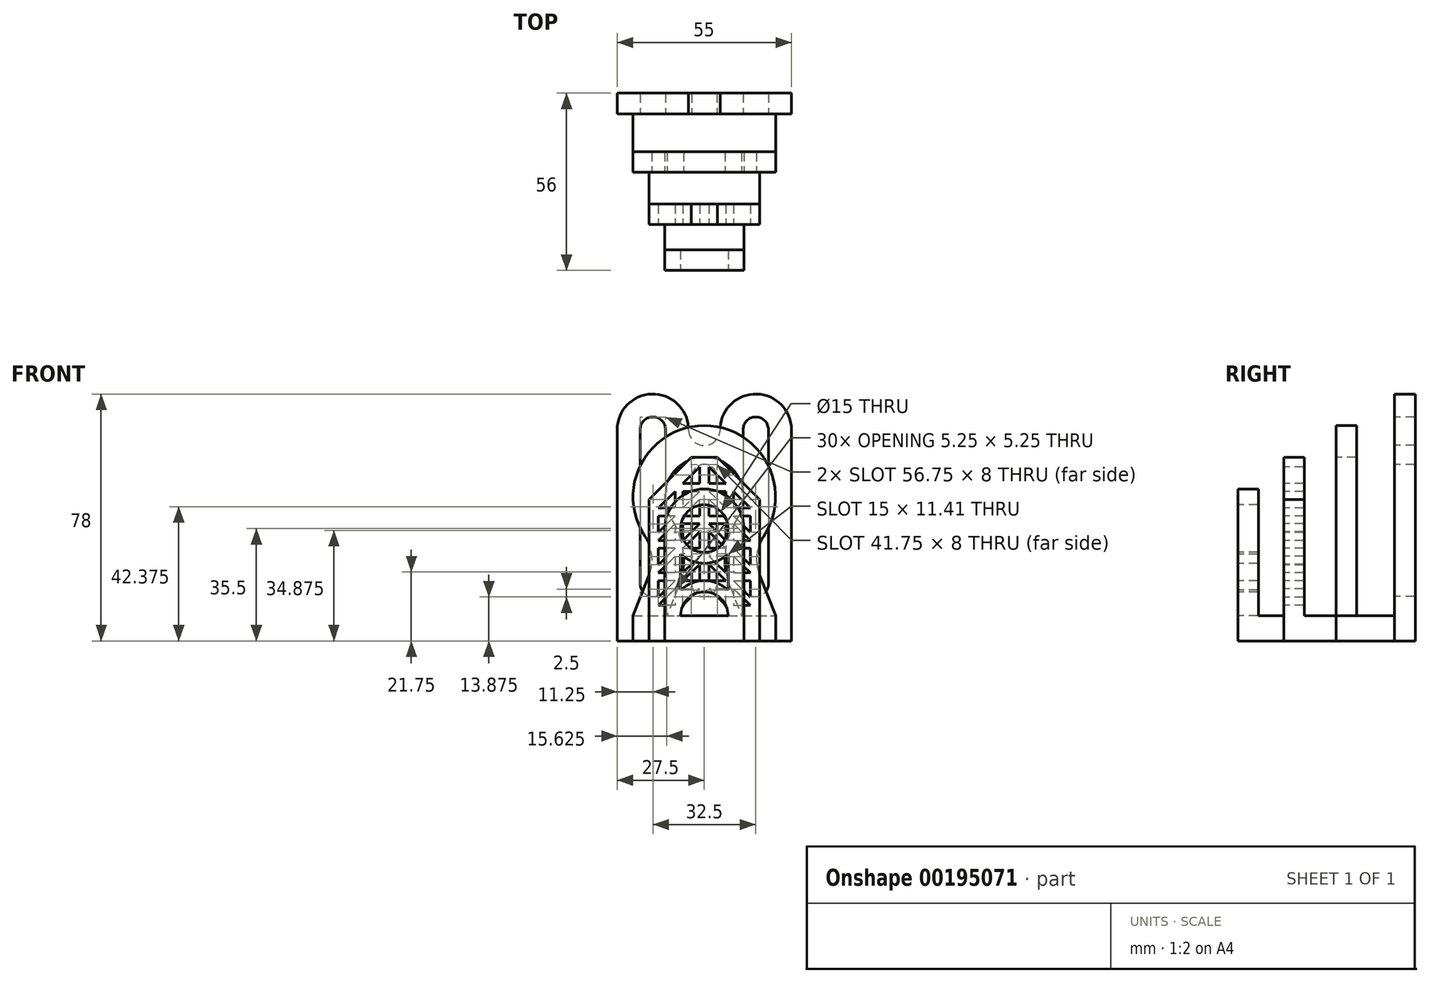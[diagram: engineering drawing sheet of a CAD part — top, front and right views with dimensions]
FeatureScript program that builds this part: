
annotation { "Feature Type Name" : "Feature", "Feature Type Description" : "" }
export const myFeature = defineFeature(function(context is Context, id is Id, definition is map)
    precondition{}
    {
        {
            var Q0;
            Q0=qCreatedBy(makeId("Front.planeOp"),FACE);
            var sketch = newSketch(context, id + "F0", { "sketchPlane" : qUnion([Q0])});
            skLineSegment(sketch, "E0.bottom", {"start": v(-12.5, 0) * mm, "end": v(-7.5, 0) * mm});
            skLineSegment(sketch, "E0.left", {"start": v(-12.5, 0) * mm, "end": v(-12.5, 27.5) * mm});
            skLineSegment(sketch, "E0.right", {"start": v(12.5, 0) * mm, "end": v(12.5, 27.5) * mm});
            skPoint(sketch, "E1", {"position": v(0, 0) * mm});
            skArc(sketch, "E2", {"start": v(12.5, 27.5) * mm, "mid": v(0, 40) * mm, "end": v(-12.5, 27.5) * mm});
            skPoint(sketch, "E3", {"position": v(0, 40) * mm});
            skCircle(sketch, "E4", {"center": v(0, 27.5) * mm, "radius": 7.5 * mm});
            skArc(sketch, "E5", {"start": v(7.5, 0) * mm, "mid": v(0, 7.5) * mm, "end": v(-7.5, 0) * mm});
            skLineSegment(sketch, "E6", {"start": v(-7.5, 27.5) * mm, "end": v(-7.5, 19.45) * mm, "construction": true});
            skLineSegment(sketch, "E7", {"start": v(0, 13.75) * mm, "end": v(-7.5, 13.75) * mm, "construction": true});
            skLineSegment(sketch, "E8", {"start": v(0, 27.5) * mm, "end": v(0, 0) * mm, "construction": true});
            skArc(sketch, "E9", {"start": v(-7.5, 19.45) * mm, "mid": v(-4.03, 17.26) * mm, "end": v(0, 16.5) * mm});
            skPoint(sketch, "E10", {"position": v(0, 20) * mm});
            skLineSegment(sketch, "E11", {"start": v(-7.5, 19.45) * mm, "end": v(-7.5, 13.75) * mm});
            skLineSegment(sketch, "E12", {"start": v(-7.5, 13.75) * mm, "end": v(-7.5, 8.05) * mm});
            skArc(sketch, "E13.MirrorCS", {"start": v(-7.5, 8.05) * mm, "mid": v(-4.03, 10.24) * mm, "end": v(0, 11) * mm});
            skLineSegment(sketch, "E14", {"start": v(-7.5, 8.05) * mm, "end": v(-7.5, 0) * mm, "construction": true});
            skArc(sketch, "E15.MirrorCS", {"start": v(7.5, 19.45) * mm, "mid": v(4.03, 17.26) * mm, "end": v(0, 16.5) * mm});
            skLineSegment(sketch, "E16.MirrorCS", {"start": v(7.5, 19.45) * mm, "end": v(7.5, 13.75) * mm});
            skLineSegment(sketch, "E17.MirrorCS", {"start": v(7.5, 13.75) * mm, "end": v(7.5, 8.05) * mm});
            skArc(sketch, "E18.MirrorCS", {"start": v(7.5, 8.05) * mm, "mid": v(4.03, 10.24) * mm, "end": v(0, 11) * mm});
            skLineSegment(sketch, "E19.trimOffspring", {"start": v(7.5, 0) * mm, "end": v(12.5, 0) * mm});
            skSolve(sketch);
        }
        {
            var Q0;
            Q0 = qSketchRegion(id + "F0", true);
            extrude(context, id + "F1", {"entities" : qUnion([Q0]), "oppositeDirection" : true, "depth" : 6.5 * mm});
        }
        {
            var Q0;
            Q0=makeQuery(id+"F1.opExtrude","CAP_FACE",FACE,{"disambiguationData":[OSD([sQuery(id+"F0.wireOp",EDGE,"E0.bottom"),sQuery(id+"F0.wireOp",EDGE,"E0.top"),sQuery(id+"F0.wireOp",EDGE,"E0.left"),sQuery(id+"F0.wireOp",EDGE,"E0.right")])],"isStart":false});
            cPlane(context, id + "F2", {"entities" : qUnion([Q0]), "cplaneType" : CPlaneType.OFFSET, "offset" : 8 * mm, "width" : 150 * mm, "height" : 150 * mm});
        }
        {
            var Q0;
            Q0=qCreatedBy(id+"F2.planeOp",FACE);
            var sketch = newSketch(context, id + "F3", { "sketchPlane" : qUnion([Q0])});
            skLineSegment(sketch, "E20.bottom", {"start": v(17.5, 0) * mm, "end": v(-17.5, 0) * mm});
            skPoint(sketch, "E21", {"position": v(0, 0) * mm});
            skLineSegment(sketch, "E22", {"start": v(-4.16, 50) * mm, "end": v(-17.5, 36.66) * mm});
            skLineSegment(sketch, "E23", {"start": v(-17.5, 36.66) * mm, "end": v(-17.5, 0) * mm});
            skPoint(sketch, "E24", {"position": v(-17.5, 50) * mm});
            skLineSegment(sketch, "E25", {"start": v(-4.16, 50) * mm, "end": v(0, 50) * mm});
            skLineSegment(sketch, "E26", {"start": v(-6.75, 39.25) * mm, "end": v(-1.5, 39.25) * mm});
            skLineSegment(sketch, "E27", {"start": v(-1.5, 39.25) * mm, "end": v(-6.75, 34) * mm});
            skLineSegment(sketch, "E28", {"start": v(-6.75, 34) * mm, "end": v(-6.75, 39.25) * mm});
            skLineSegment(sketch, "E29", {"start": v(-9.25, 39.25) * mm, "end": v(-9.25, 34) * mm});
            skLineSegment(sketch, "E30", {"start": v(-9.25, 34) * mm, "end": v(-14.5, 34) * mm});
            skLineSegment(sketch, "E31", {"start": v(-14.5, 34) * mm, "end": v(-9.25, 39.25) * mm});
            skLineSegment(sketch, "E32", {"start": v(-9.25, 31.5) * mm, "end": v(-14.5, 31.5) * mm});
            skLineSegment(sketch, "E33", {"start": v(-14.5, 31.5) * mm, "end": v(-14.5, 26.25) * mm});
            skLineSegment(sketch, "E34", {"start": v(-14.5, 26.25) * mm, "end": v(-9.25, 31.5) * mm});
            skLineSegment(sketch, "E35", {"start": v(-6.75, 41.75) * mm, "end": v(-1.5, 41.75) * mm});
            skLineSegment(sketch, "E36", {"start": v(-1.5, 41.75) * mm, "end": v(-1.5, 47) * mm});
            skLineSegment(sketch, "E37", {"start": v(-1.5, 47) * mm, "end": v(-6.75, 41.75) * mm});
            skLineSegment(sketch, "E38", {"start": v(-6.75, 34) * mm, "end": v(-9.25, 31.5) * mm, "construction": true});
            skLineSegment(sketch, "E39", {"start": v(-6.75, 41.75) * mm, "end": v(-9.25, 39.25) * mm, "construction": true});
            skLineSegment(sketch, "E40.direction1", {"start": v(-6.75, 41.75) * mm, "end": v(-6.75, 31.5) * mm, "construction": true});
            skLineSegment(sketch, "E41.0.1.0", {"start": v(-1.5, 36.75) * mm, "end": v(-6.75, 31.5) * mm});
            skLineSegment(sketch, "E41.3.1.0", {"start": v(-1.5, 31.5) * mm, "end": v(-1.5, 36.75) * mm});
            skLineSegment(sketch, "E41.6.1.0", {"start": v(-6.75, 31.5) * mm, "end": v(-1.5, 31.5) * mm});
            skLineSegment(sketch, "E41.9.1.0", {"start": v(-6.75, 29) * mm, "end": v(-1.5, 29) * mm});
            skLineSegment(sketch, "E41.12.1.0", {"start": v(-1.5, 29) * mm, "end": v(-6.75, 23.75) * mm});
            skLineSegment(sketch, "E41.15.1.0", {"start": v(-6.75, 23.75) * mm, "end": v(-6.75, 29) * mm});
            skLineSegment(sketch, "E41.18.1.0", {"start": v(-9.25, 29) * mm, "end": v(-9.25, 23.75) * mm});
            skLineSegment(sketch, "E41.21.1.0", {"start": v(-14.5, 23.75) * mm, "end": v(-9.25, 29) * mm});
            skLineSegment(sketch, "E41.24.1.0", {"start": v(-9.25, 23.75) * mm, "end": v(-14.5, 23.75) * mm});
            skLineSegment(sketch, "E41.27.1.0", {"start": v(-9.25, 21.25) * mm, "end": v(-14.5, 21.25) * mm});
            skLineSegment(sketch, "E41.30.1.0", {"start": v(-14.5, 16) * mm, "end": v(-9.25, 21.25) * mm});
            skLineSegment(sketch, "E41.33.1.0", {"start": v(-14.5, 21.25) * mm, "end": v(-14.5, 16) * mm});
            skLineSegment(sketch, "E41.0.2.0", {"start": v(-1.5, 26.5) * mm, "end": v(-6.75, 21.25) * mm});
            skLineSegment(sketch, "E41.3.2.0", {"start": v(-1.5, 21.25) * mm, "end": v(-1.5, 26.5) * mm});
            skLineSegment(sketch, "E41.6.2.0", {"start": v(-6.75, 21.25) * mm, "end": v(-1.5, 21.25) * mm});
            skLineSegment(sketch, "E41.9.2.0", {"start": v(-6.75, 18.75) * mm, "end": v(-1.5, 18.75) * mm});
            skLineSegment(sketch, "E41.12.2.0", {"start": v(-1.5, 18.75) * mm, "end": v(-6.75, 13.5) * mm});
            skLineSegment(sketch, "E41.15.2.0", {"start": v(-6.75, 13.5) * mm, "end": v(-6.75, 18.75) * mm});
            skLineSegment(sketch, "E41.18.2.0", {"start": v(-9.25, 18.75) * mm, "end": v(-9.25, 13.5) * mm});
            skLineSegment(sketch, "E41.21.2.0", {"start": v(-14.5, 13.5) * mm, "end": v(-9.25, 18.75) * mm});
            skLineSegment(sketch, "E41.24.2.0", {"start": v(-9.25, 13.5) * mm, "end": v(-14.5, 13.5) * mm});
            skLineSegment(sketch, "E41.27.2.0", {"start": v(-9.25, 11) * mm, "end": v(-14.5, 11) * mm});
            skLineSegment(sketch, "E41.30.2.0", {"start": v(-14.5, 5.75) * mm, "end": v(-9.25, 11) * mm});
            skLineSegment(sketch, "E41.33.2.0", {"start": v(-14.5, 11) * mm, "end": v(-14.5, 5.75) * mm});
            skLineSegment(sketch, "E41.0.3.0", {"start": v(-1.5, 16.25) * mm, "end": v(-6.75, 11) * mm});
            skLineSegment(sketch, "E41.3.3.0", {"start": v(-1.5, 11) * mm, "end": v(-1.5, 16.25) * mm});
            skLineSegment(sketch, "E41.6.3.0", {"start": v(-6.75, 11) * mm, "end": v(-1.5, 11) * mm});
            skLineSegment(sketch, "E41.9.3.0", {"start": v(-6.75, 8.5) * mm, "end": v(-1.5, 8.5) * mm});
            skLineSegment(sketch, "E41.12.3.0", {"start": v(-1.5, 8.5) * mm, "end": v(-6.75, 3.25) * mm});
            skLineSegment(sketch, "E41.15.3.0", {"start": v(-6.75, 3.25) * mm, "end": v(-6.75, 8.5) * mm});
            skLineSegment(sketch, "E41.18.3.0", {"start": v(-9.25, 8.5) * mm, "end": v(-9.25, 3.25) * mm});
            skLineSegment(sketch, "E41.21.3.0", {"start": v(-14.5, 3.25) * mm, "end": v(-9.25, 8.5) * mm});
            skLineSegment(sketch, "E41.24.3.0", {"start": v(-9.25, 3.25) * mm, "end": v(-14.5, 3.25) * mm});
            skLineSegment(sketch, "E42.MirrorCS", {"start": v(4.16, 50) * mm, "end": v(0, 50) * mm});
            skLineSegment(sketch, "E43.MirrorCS", {"start": v(4.16, 50) * mm, "end": v(17.5, 36.66) * mm});
            skLineSegment(sketch, "E44.MirrorCS", {"start": v(17.5, 36.66) * mm, "end": v(17.5, 0) * mm});
            skLineSegment(sketch, "E45.MirrorCS", {"start": v(1.5, 47) * mm, "end": v(6.75, 41.75) * mm});
            skLineSegment(sketch, "E46.MirrorCS", {"start": v(1.5, 41.75) * mm, "end": v(1.5, 47) * mm});
            skLineSegment(sketch, "E47.MirrorCS", {"start": v(6.75, 41.75) * mm, "end": v(1.5, 41.75) * mm});
            skLineSegment(sketch, "E48.MirrorCS", {"start": v(6.75, 39.25) * mm, "end": v(1.5, 39.25) * mm});
            skLineSegment(sketch, "E49.MirrorCS", {"start": v(1.5, 39.25) * mm, "end": v(6.75, 34) * mm});
            skLineSegment(sketch, "E50.MirrorCS", {"start": v(9.25, 39.25) * mm, "end": v(9.25, 34) * mm});
            skLineSegment(sketch, "E51.MirrorCS", {"start": v(14.5, 34) * mm, "end": v(9.25, 39.25) * mm});
            skLineSegment(sketch, "E52.MirrorCS", {"start": v(9.25, 34) * mm, "end": v(14.5, 34) * mm});
            skLineSegment(sketch, "E53.MirrorCS", {"start": v(1.5, 36.75) * mm, "end": v(6.75, 31.5) * mm});
            skLineSegment(sketch, "E54.MirrorCS", {"start": v(1.5, 31.5) * mm, "end": v(1.5, 36.75) * mm});
            skLineSegment(sketch, "E55.MirrorCS", {"start": v(6.75, 31.5) * mm, "end": v(1.5, 31.5) * mm});
            skLineSegment(sketch, "E56.MirrorCS", {"start": v(9.25, 31.5) * mm, "end": v(14.5, 31.5) * mm});
            skLineSegment(sketch, "E57.MirrorCS", {"start": v(14.5, 26.25) * mm, "end": v(9.25, 31.5) * mm});
            skLineSegment(sketch, "E58.MirrorCS", {"start": v(14.5, 31.5) * mm, "end": v(14.5, 26.25) * mm});
            skLineSegment(sketch, "E59.MirrorCS", {"start": v(6.75, 29) * mm, "end": v(1.5, 29) * mm});
            skLineSegment(sketch, "E60.MirrorCS", {"start": v(1.5, 29) * mm, "end": v(6.75, 23.75) * mm});
            skLineSegment(sketch, "E61.MirrorCS", {"start": v(6.75, 23.75) * mm, "end": v(6.75, 29) * mm});
            skLineSegment(sketch, "E62.MirrorCS", {"start": v(9.25, 29) * mm, "end": v(9.25, 23.75) * mm});
            skLineSegment(sketch, "E63.MirrorCS", {"start": v(14.5, 23.75) * mm, "end": v(9.25, 29) * mm});
            skLineSegment(sketch, "E64.MirrorCS", {"start": v(9.25, 23.75) * mm, "end": v(14.5, 23.75) * mm});
            skLineSegment(sketch, "E65.MirrorCS", {"start": v(1.5, 26.5) * mm, "end": v(6.75, 21.25) * mm});
            skLineSegment(sketch, "E66.MirrorCS", {"start": v(1.5, 21.25) * mm, "end": v(1.5, 26.5) * mm});
            skLineSegment(sketch, "E67.MirrorCS", {"start": v(6.75, 21.25) * mm, "end": v(1.5, 21.25) * mm});
            skLineSegment(sketch, "E68.MirrorCS", {"start": v(9.25, 21.25) * mm, "end": v(14.5, 21.25) * mm});
            skLineSegment(sketch, "E69.MirrorCS", {"start": v(14.5, 16) * mm, "end": v(9.25, 21.25) * mm});
            skLineSegment(sketch, "E70.MirrorCS", {"start": v(14.5, 21.25) * mm, "end": v(14.5, 16) * mm});
            skLineSegment(sketch, "E71.MirrorCS", {"start": v(6.75, 18.75) * mm, "end": v(1.5, 18.75) * mm});
            skLineSegment(sketch, "E72.MirrorCS", {"start": v(1.5, 18.75) * mm, "end": v(6.75, 13.5) * mm});
            skLineSegment(sketch, "E73.MirrorCS", {"start": v(6.75, 13.5) * mm, "end": v(6.75, 18.75) * mm});
            skLineSegment(sketch, "E74.MirrorCS", {"start": v(9.25, 18.75) * mm, "end": v(9.25, 13.5) * mm});
            skLineSegment(sketch, "E75.MirrorCS", {"start": v(14.5, 13.5) * mm, "end": v(9.25, 18.75) * mm});
            skLineSegment(sketch, "E76.MirrorCS", {"start": v(9.25, 13.5) * mm, "end": v(14.5, 13.5) * mm});
            skLineSegment(sketch, "E77.MirrorCS", {"start": v(1.5, 16.25) * mm, "end": v(6.75, 11) * mm});
            skLineSegment(sketch, "E78.MirrorCS", {"start": v(1.5, 11) * mm, "end": v(1.5, 16.25) * mm});
            skLineSegment(sketch, "E79.MirrorCS", {"start": v(6.75, 11) * mm, "end": v(1.5, 11) * mm});
            skLineSegment(sketch, "E80.MirrorCS", {"start": v(9.25, 11) * mm, "end": v(14.5, 11) * mm});
            skLineSegment(sketch, "E81.MirrorCS", {"start": v(14.5, 5.75) * mm, "end": v(9.25, 11) * mm});
            skLineSegment(sketch, "E82.MirrorCS", {"start": v(14.5, 11) * mm, "end": v(14.5, 5.75) * mm});
            skLineSegment(sketch, "E83.MirrorCS", {"start": v(14.5, 3.25) * mm, "end": v(9.25, 8.5) * mm});
            skLineSegment(sketch, "E84.MirrorCS", {"start": v(9.25, 8.5) * mm, "end": v(9.25, 3.25) * mm});
            skLineSegment(sketch, "E85.MirrorCS", {"start": v(9.25, 3.25) * mm, "end": v(14.5, 3.25) * mm});
            skLineSegment(sketch, "E86.MirrorCS", {"start": v(6.75, 3.25) * mm, "end": v(6.75, 8.5) * mm});
            skLineSegment(sketch, "E87.MirrorCS", {"start": v(6.75, 8.5) * mm, "end": v(1.5, 8.5) * mm});
            skLineSegment(sketch, "E88.MirrorCS", {"start": v(1.5, 8.5) * mm, "end": v(6.75, 3.25) * mm});
            skLineSegment(sketch, "E89", {"start": v(6.75, 39.25) * mm, "end": v(6.75, 34) * mm});
            skSolve(sketch);
        }
        {
            var Q0;
            Q0 = qSketchRegion(id + "F3", true);
            extrude(context, id + "F4", {"entities" : qUnion([Q0]), "depth" : 6.5 * mm});
        }
        {
            var Q0;
            Q0=makeQuery(id+"F4.opExtrude","CAP_FACE",FACE,{"disambiguationData":[OSD([sQuery(id+"F3.wireOp",EDGE,"E20.bottom"),sQuery(id+"F3.wireOp",EDGE,"E20.top"),sQuery(id+"F3.wireOp",EDGE,"E20.left"),sQuery(id+"F3.wireOp",EDGE,"E20.right")])],"isStart":false});
            cPlane(context, id + "F5", {"entities" : qUnion([Q0]), "cplaneType" : CPlaneType.OFFSET, "offset" : 10 * mm, "width" : 150 * mm, "height" : 150 * mm});
        }
        {
            var Q0;
            Q0=qCreatedBy(id+"F5.planeOp",FACE);
            var sketch = newSketch(context, id + "F6", { "sketchPlane" : qUnion([Q0])});
            skLineSegment(sketch, "E90.top", {"start": v(22.5, 0) * mm, "end": v(-22.5, 0) * mm, "construction": true});
            skPoint(sketch, "E91", {"position": v(0, 0) * mm});
            skPoint(sketch, "E92", {"position": v(-22.5, 60) * mm});
            skArc(sketch, "E93", {"start": v(0, 60) * mm, "mid": v(-19.85, 48.1) * mm, "end": v(-18.7, 24.99) * mm});
            skPoint(sketch, "E94", {"position": v(-22.5, 37.5) * mm});
            skArc(sketch, "E95", {"start": v(-17.4, 12.99) * mm, "mid": v(-16.58, 19.15) * mm, "end": v(-18.7, 24.99) * mm});
            skLineSegment(sketch, "E96", {"start": v(-17.4, 12.99) * mm, "end": v(-22.5, 0) * mm});
            skPoint(sketch, "E97", {"position": v(-16.5, 17.75) * mm});
            skPoint(sketch, "E98", {"position": v(0, 51) * mm});
            skArc(sketch, "E99.0", {"start": v(-8.1, 9.33) * mm, "mid": v(-6.63, 20.22) * mm, "end": v(-10.39, 30.55) * mm});
            skArc(sketch, "E99.1", {"start": v(0, 50) * mm, "mid": v(-11.03, 43.39) * mm, "end": v(-10.39, 30.55) * mm});
            skLineSegment(sketch, "E100", {"start": v(-8.1, 9.33) * mm, "end": v(-11.76, 0) * mm});
            skLineSegment(sketch, "E101", {"start": v(-11.76, 0) * mm, "end": v(-22.5, 0) * mm});
            skLineSegment(sketch, "E102", {"start": v(-29.52, 17.75) * mm, "end": v(-8.1, 9.33) * mm, "construction": true});
            skArc(sketch, "E103.MirrorCS", {"start": v(0, 50) * mm, "mid": v(11.03, 43.39) * mm, "end": v(10.39, 30.55) * mm});
            skArc(sketch, "E104.MirrorCS", {"start": v(8.1, 9.33) * mm, "mid": v(6.63, 20.22) * mm, "end": v(10.39, 30.55) * mm});
            skLineSegment(sketch, "E105.MirrorCS", {"start": v(8.1, 9.33) * mm, "end": v(11.76, 0) * mm});
            skLineSegment(sketch, "E106.MirrorCS", {"start": v(17.4, 12.99) * mm, "end": v(22.5, 0) * mm});
            skArc(sketch, "E107.MirrorCS", {"start": v(17.4, 12.99) * mm, "mid": v(16.58, 19.15) * mm, "end": v(18.7, 24.99) * mm});
            skArc(sketch, "E108.MirrorCS", {"start": v(0, 60) * mm, "mid": v(19.85, 48.1) * mm, "end": v(18.7, 24.99) * mm});
            skLineSegment(sketch, "E109", {"start": v(22.5, 0) * mm, "end": v(11.76, 0) * mm});
            skSolve(sketch);
        }
        {
            var Q0;
            Q0 = qSketchRegion(id + "F6", true);
            extrude(context, id + "F7", {"entities" : qUnion([Q0]), "depth" : 6.5 * mm});
        }
        {
            var Q0;
            Q0=makeQuery(id+"F7.opExtrude","CAP_FACE",FACE,{"disambiguationData":[OSD([sQuery(id+"F6.wireOp",EDGE,"E93"),sQuery(id+"F6.wireOp",EDGE,"E95"),sQuery(id+"F6.wireOp",EDGE,"E96"),sQuery(id+"F6.wireOp",EDGE,"E99.0"),sQuery(id+"F6.wireOp",EDGE,"E99.1"),sQuery(id+"F6.wireOp",EDGE,"E100"),sQuery(id+"F6.wireOp",EDGE,"E103.MirrorCS"),sQuery(id+"F6.wireOp",EDGE,"E104.MirrorCS"),sQuery(id+"F6.wireOp",EDGE,"E105.MirrorCS"),sQuery(id+"F6.wireOp",EDGE,"E106.MirrorCS"),sQuery(id+"F6.wireOp",EDGE,"E107.MirrorCS"),sQuery(id+"F6.wireOp",EDGE,"E108.MirrorCS"),sQuery(id+"F6.wireOp",EDGE,"E109"),sQuery(id+"F6.wireOp",EDGE,"E101")])],"isStart":false});
            cPlane(context, id + "F8", {"entities" : qUnion([Q0]), "cplaneType" : CPlaneType.OFFSET, "offset" : 12 * mm, "width" : 150 * mm, "height" : 150 * mm});
        }
        {
            var Q0;
            Q0=qCreatedBy(id+"F8.planeOp",FACE);
            var sketch = newSketch(context, id + "F9", { "sketchPlane" : qUnion([Q0])});
            skLineSegment(sketch, "E110.bottom", {"start": v(27.5, 0) * mm, "end": v(-27.5, 0) * mm});
            skPoint(sketch, "E111", {"position": v(0, 0) * mm});
            skPoint(sketch, "E112", {"position": v(-27.5, 70) * mm});
            skArc(sketch, "E113", {"start": v(-5, 58.75) * mm, "mid": v(-16.25, 70) * mm, "end": v(-27.5, 58.75) * mm});
            skPoint(sketch, "E114", {"position": v(-27.5, 58.75) * mm});
            skPoint(sketch, "E115", {"position": v(-16.25, 70) * mm});
            skArc(sketch, "E116", {"start": v(-5, 58.75) * mm, "mid": v(-3.54, 55.21) * mm, "end": v(0, 53.75) * mm});
            skLineSegment(sketch, "E117", {"start": v(-27.5, 58.75) * mm, "end": v(-27.5, 0) * mm});
            skArc(sketch, "E118", {"start": v(-12.25, 58.75) * mm, "mid": v(-16.25, 62.75) * mm, "end": v(-20.25, 58.75) * mm});
            skLineSegment(sketch, "E119", {"start": v(-20.25, 58.75) * mm, "end": v(-20.25, 10) * mm});
            skLineSegment(sketch, "E120", {"start": v(-12.25, 58.75) * mm, "end": v(-12.25, 10) * mm});
            skArc(sketch, "E121", {"start": v(-20.25, 10) * mm, "mid": v(-16.25, 6) * mm, "end": v(-12.25, 10) * mm});
            skArc(sketch, "E122", {"start": v(0, 47.75) * mm, "mid": v(-2.83, 46.58) * mm, "end": v(-4, 43.75) * mm});
            skArc(sketch, "E123", {"start": v(-4, 10) * mm, "mid": v(-2.83, 7.17) * mm, "end": v(0, 6) * mm});
            skLineSegment(sketch, "E124", {"start": v(-4, 43.75) * mm, "end": v(-4, 10) * mm});
            skPoint(sketch, "E125", {"position": v(-16.25, 6) * mm});
            skArc(sketch, "E126.MirrorCS", {"start": v(5, 58.75) * mm, "mid": v(3.54, 55.21) * mm, "end": v(0, 53.75) * mm});
            skArc(sketch, "E127.MirrorCS", {"start": v(5, 58.75) * mm, "mid": v(16.25, 70) * mm, "end": v(27.5, 58.75) * mm});
            skLineSegment(sketch, "E128.MirrorCS", {"start": v(27.5, 58.75) * mm, "end": v(27.5, 0) * mm});
            skLineSegment(sketch, "E129.MirrorCS", {"start": v(20.25, 58.75) * mm, "end": v(20.25, 10) * mm});
            skArc(sketch, "E130.MirrorCS", {"start": v(12.25, 58.75) * mm, "mid": v(16.25, 62.75) * mm, "end": v(20.25, 58.75) * mm});
            skLineSegment(sketch, "E131.MirrorCS", {"start": v(12.25, 58.75) * mm, "end": v(12.25, 10) * mm});
            skArc(sketch, "E132.MirrorCS", {"start": v(20.25, 10) * mm, "mid": v(16.25, 6) * mm, "end": v(12.25, 10) * mm});
            skArc(sketch, "E133.MirrorCS", {"start": v(4, 10) * mm, "mid": v(2.83, 7.17) * mm, "end": v(0, 6) * mm});
            skLineSegment(sketch, "E134.MirrorCS", {"start": v(4, 43.75) * mm, "end": v(4, 10) * mm});
            skArc(sketch, "E135.MirrorCS", {"start": v(0, 47.75) * mm, "mid": v(2.83, 46.58) * mm, "end": v(4, 43.75) * mm});
            skSolve(sketch);
        }
        {
            var Q0;
            Q0 = qSketchRegion(id + "F9", true);
            extrude(context, id + "F10", {"entities" : qUnion([Q0]), "depth" : 6.5 * mm});
        }
        {
            var Q0;
            Q0=qCreatedBy(makeId("Top.planeOp"),FACE);
            var sketch = newSketch(context, id + "F11", { "sketchPlane" : qUnion([Q0])});
            skLineSegment(sketch, "E136", {"start": v(0, 0) * mm, "end": v(12.5, 0) * mm});
            skLineSegment(sketch, "E137", {"start": v(12.5, 0) * mm, "end": v(12.5, 6.5) * mm});
            skLineSegment(sketch, "E138", {"start": v(12.5, 6.5) * mm, "end": v(12.5, 14.5) * mm});
            skLineSegment(sketch, "E139", {"start": v(12.5, 14.5) * mm, "end": v(17.5, 14.5) * mm});
            skLineSegment(sketch, "E140", {"start": v(17.5, 14.5) * mm, "end": v(17.5, 21) * mm});
            skLineSegment(sketch, "E141", {"start": v(17.5, 21) * mm, "end": v(17.5, 31) * mm});
            skLineSegment(sketch, "E142", {"start": v(-22.5, 31) * mm, "end": v(-22.5, 37.5) * mm});
            skLineSegment(sketch, "E143", {"start": v(-22.5, 37.5) * mm, "end": v(-22.5, 49.5) * mm});
            skLineSegment(sketch, "E144", {"start": v(-27.5, 49.5) * mm, "end": v(-22.5, 49.5) * mm});
            skLineSegment(sketch, "E145", {"start": v(-27.5, 49.5) * mm, "end": v(-27.5, 56) * mm});
            skLineSegment(sketch, "E146", {"start": v(0, 56) * mm, "end": v(-27.5, 56) * mm});
            skLineSegment(sketch, "E147.MirrorCS", {"start": v(0, 0) * mm, "end": v(-12.5, 0) * mm});
            skLineSegment(sketch, "E148.MirrorCS", {"start": v(-12.5, 0) * mm, "end": v(-12.5, 6.5) * mm});
            skLineSegment(sketch, "E149.MirrorCS", {"start": v(-12.5, 6.5) * mm, "end": v(-12.5, 14.5) * mm});
            skLineSegment(sketch, "E150.MirrorCS", {"start": v(-12.5, 14.5) * mm, "end": v(-17.5, 14.5) * mm});
            skLineSegment(sketch, "E151.MirrorCS", {"start": v(-17.5, 14.5) * mm, "end": v(-17.5, 21) * mm});
            skLineSegment(sketch, "E152.MirrorCS", {"start": v(-17.5, 21) * mm, "end": v(-17.5, 31) * mm});
            skLineSegment(sketch, "E153.MirrorCS", {"start": v(22.5, 31) * mm, "end": v(22.5, 37.5) * mm});
            skLineSegment(sketch, "E154.MirrorCS", {"start": v(22.5, 37.5) * mm, "end": v(22.5, 49.5) * mm});
            skLineSegment(sketch, "E155.MirrorCS", {"start": v(27.5, 49.5) * mm, "end": v(22.5, 49.5) * mm});
            skLineSegment(sketch, "E156.MirrorCS", {"start": v(27.5, 49.5) * mm, "end": v(27.5, 56) * mm});
            skLineSegment(sketch, "E157.MirrorCS", {"start": v(0, 56) * mm, "end": v(27.5, 56) * mm});
            skLineSegment(sketch, "E158", {"start": v(17.5, 31) * mm, "end": v(22.5, 31) * mm});
            skLineSegment(sketch, "E159", {"start": v(-17.5, 31) * mm, "end": v(-22.5, 31) * mm});
            skSolve(sketch);
        }
        {
            var Q0;
            Q0 = qSketchRegion(id + "F11", true);
            extrude(context, id + "F12", {"entities" : qUnion([Q0]), "operationType" : NewBodyOperationType.ADD, "oppositeDirection" : true, "depth" : 8 * mm});
        }
    });
